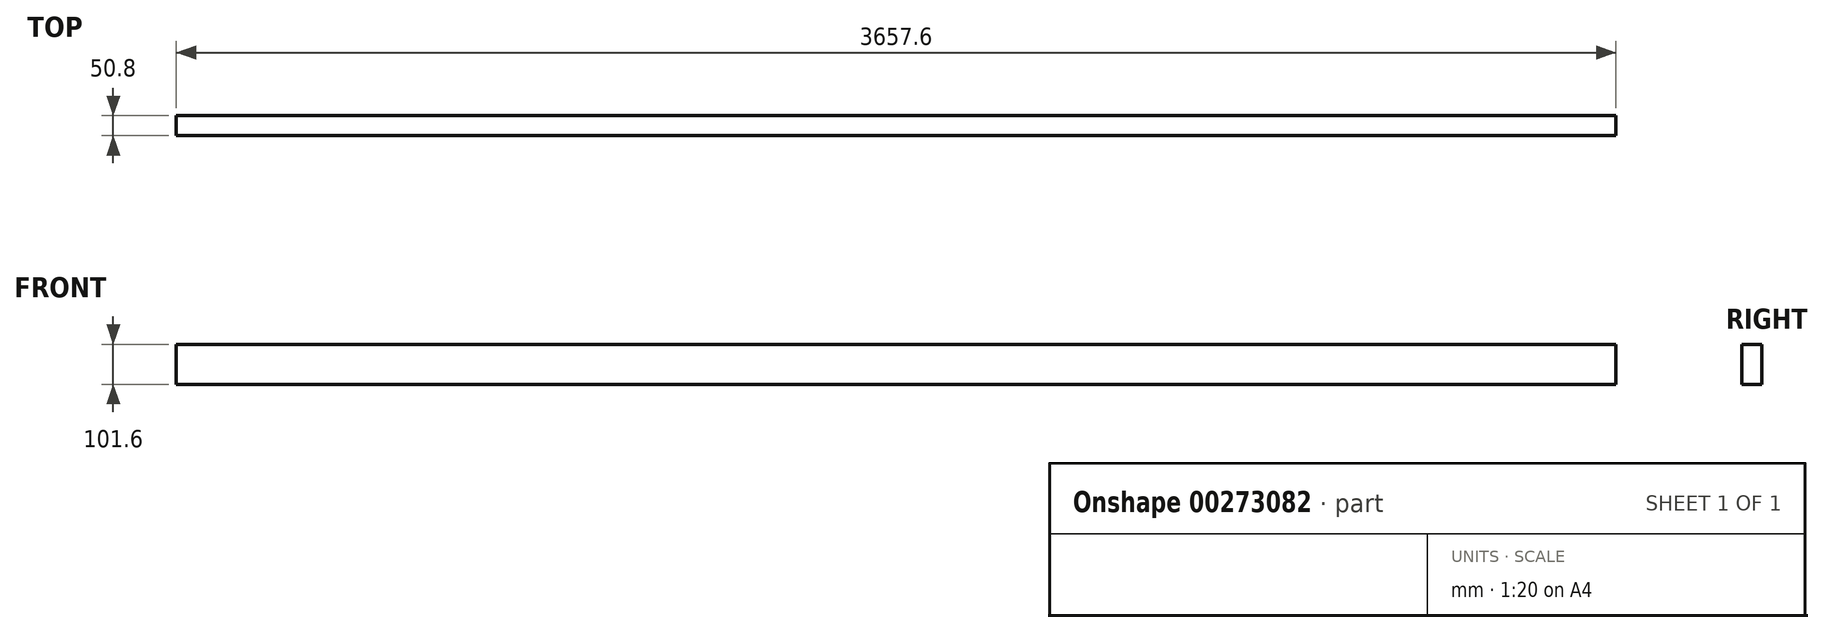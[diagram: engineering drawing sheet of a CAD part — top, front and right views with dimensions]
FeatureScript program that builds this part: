
annotation { "Feature Type Name" : "Feature", "Feature Type Description" : "" }
export const myFeature = defineFeature(function(context is Context, id is Id, definition is map)
    precondition{}
    {
        {
            var Q0;
            Q0=qCreatedBy(makeId("Front.planeOp"),FACE);
            var sketch = newSketch(context, id + "F0", { "sketchPlane" : qUnion([Q0])});
            skLineSegment(sketch, "E0.bottom", {"start": v(-1837.06, -123.37) * mm, "end": v(1820.54, -123.37) * mm});
            skLineSegment(sketch, "E0.top", {"start": v(-1837.06, -224.97) * mm, "end": v(1820.54, -224.97) * mm});
            skLineSegment(sketch, "E0.left", {"start": v(-1837.06, -123.37) * mm, "end": v(-1837.06, -224.97) * mm});
            skLineSegment(sketch, "E0.right", {"start": v(1820.54, -123.37) * mm, "end": v(1820.54, -224.97) * mm});
            skSolve(sketch);
        }
        {
            var Q0;
            Q0 = qSketchRegion(id + "F0", true);
            extrude(context, id + "F1", {"entities" : qUnion([Q0]), "depth" : 50.8 * mm});
        }
    });
